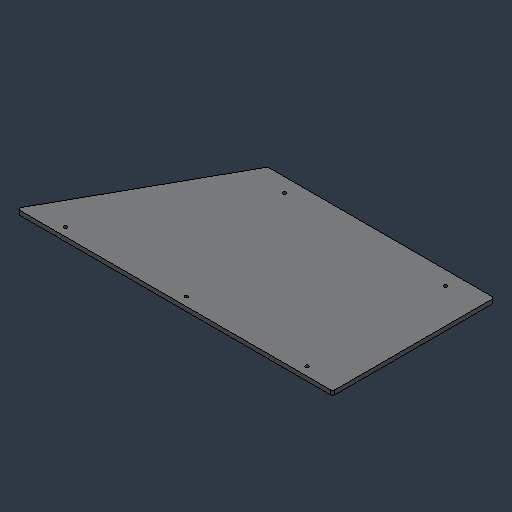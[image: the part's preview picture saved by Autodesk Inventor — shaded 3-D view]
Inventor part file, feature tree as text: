
AUTODESK INVENTOR PART (.ipt)
format: ipt  version: 2024.3 (Build 283343000, 343)  size: 85,504 bytes
history: native  units: mm (DEFAULTED — no unit token found)
features: fillet x1
ambient origin geometry x8: Origin, YZ Plane, XZ Plane, XY Plane, X Axis, Y Axis, Z Axis, Center Point
bodies: Solid1 (feature_tree)
feature tree (1):
  fillet  "Fillet1"  [1 undecoded]
note: 1 required parameter value undecoded (feature->parameter linkage not recoverable at this tier; creation-order binding heuristic only, values carry confidence <= 0.55)
